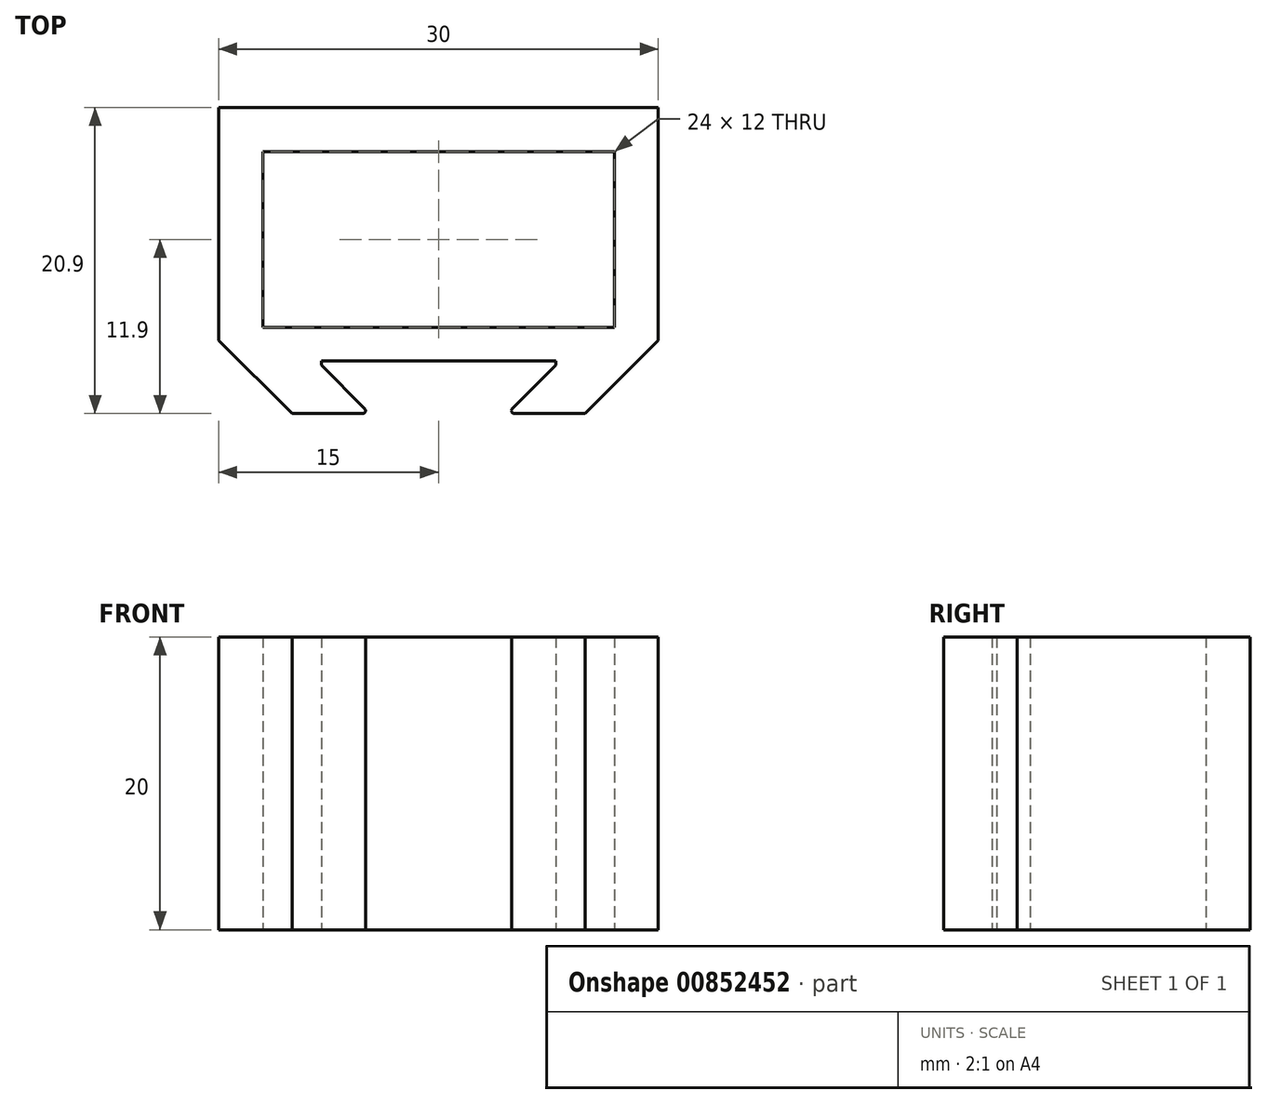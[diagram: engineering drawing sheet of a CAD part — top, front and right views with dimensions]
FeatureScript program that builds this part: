
annotation { "Feature Type Name" : "Feature", "Feature Type Description" : "" }
export const myFeature = defineFeature(function(context is Context, id is Id, definition is map)
    precondition{}
    {
        {
            var Q0;
            Q0=qCreatedBy(makeId("Top.planeOp"),FACE);
            var sketch = newSketch(context, id + "F0", { "sketchPlane" : qUnion([Q0])});
            skLineSegment(sketch, "E0.bottom", {"start": v(-15, 17.3) * mm, "end": v(15, 17.3) * mm});
            skLineSegment(sketch, "E0.left", {"start": v(-15, 17.3) * mm, "end": v(-15, 1.4) * mm});
            skLineSegment(sketch, "E0.right", {"start": v(15, 17.3) * mm, "end": v(15, 1.4) * mm});
            skLineSegment(sketch, "E1.bottom", {"start": v(-12, 14.3) * mm, "end": v(12, 14.3) * mm});
            skLineSegment(sketch, "E1.top", {"start": v(-12, 2.3) * mm, "end": v(12, 2.3) * mm});
            skLineSegment(sketch, "E1.left", {"start": v(-12, 14.3) * mm, "end": v(-12, 2.3) * mm});
            skLineSegment(sketch, "E1.right", {"start": v(12, 14.3) * mm, "end": v(12, 2.3) * mm});
            skLineSegment(sketch, "E2", {"start": v(0, 41.18) * mm, "end": v(0, -31.23) * mm, "construction": true});
            skLineSegment(sketch, "E3", {"start": v(-10, -3.6) * mm, "end": v(-5.18, -3.6) * mm});
            skLineSegment(sketch, "E4.MirrorCS", {"start": v(10, -3.6) * mm, "end": v(5.18, -3.6) * mm});
            skLineSegment(sketch, "E5", {"start": v(-5.04, -3.26) * mm, "end": v(-8, -0.3) * mm});
            skLineSegment(sketch, "E6", {"start": v(-8, -0.3) * mm, "end": v(-8, 0) * mm});
            skLineSegment(sketch, "E7.MirrorCS", {"start": v(5.04, -3.26) * mm, "end": v(8, -0.3) * mm});
            skLineSegment(sketch, "E8.MirrorCS", {"start": v(8, -0.3) * mm, "end": v(8, 0) * mm});
            skLineSegment(sketch, "E9", {"start": v(-8, 0) * mm, "end": v(8, 0) * mm});
            skPoint(sketch, "E10.visualSharp", {"position": v(-4.7, -3.6) * mm});
            skArc(sketch, "E10.filletArc", {"start": v(-5.18, -3.6) * mm, "mid": v(-5, -3.48) * mm, "end": v(-5.04, -3.26) * mm});
            skPoint(sketch, "E11.visualSharp", {"position": v(4.7, -3.6) * mm});
            skArc(sketch, "E11.filletArc", {"start": v(5.04, -3.26) * mm, "mid": v(5, -3.48) * mm, "end": v(5.18, -3.6) * mm});
            skLineSegment(sketch, "E12", {"start": v(-10, -3.6) * mm, "end": v(-15, 1.4) * mm});
            skLineSegment(sketch, "E13.MirrorCS", {"start": v(10, -3.6) * mm, "end": v(15, 1.4) * mm});
            skSolve(sketch);
        }
        {
            var Q0;
            Q0 = qSketchRegion(id + "F0", true);
            extrude(context, id + "F1", {"entities" : qUnion([Q0]), "depth" : 20 * mm, "offsetDistance" : 25 * mm, "symmetric" : true});
        }
    });
